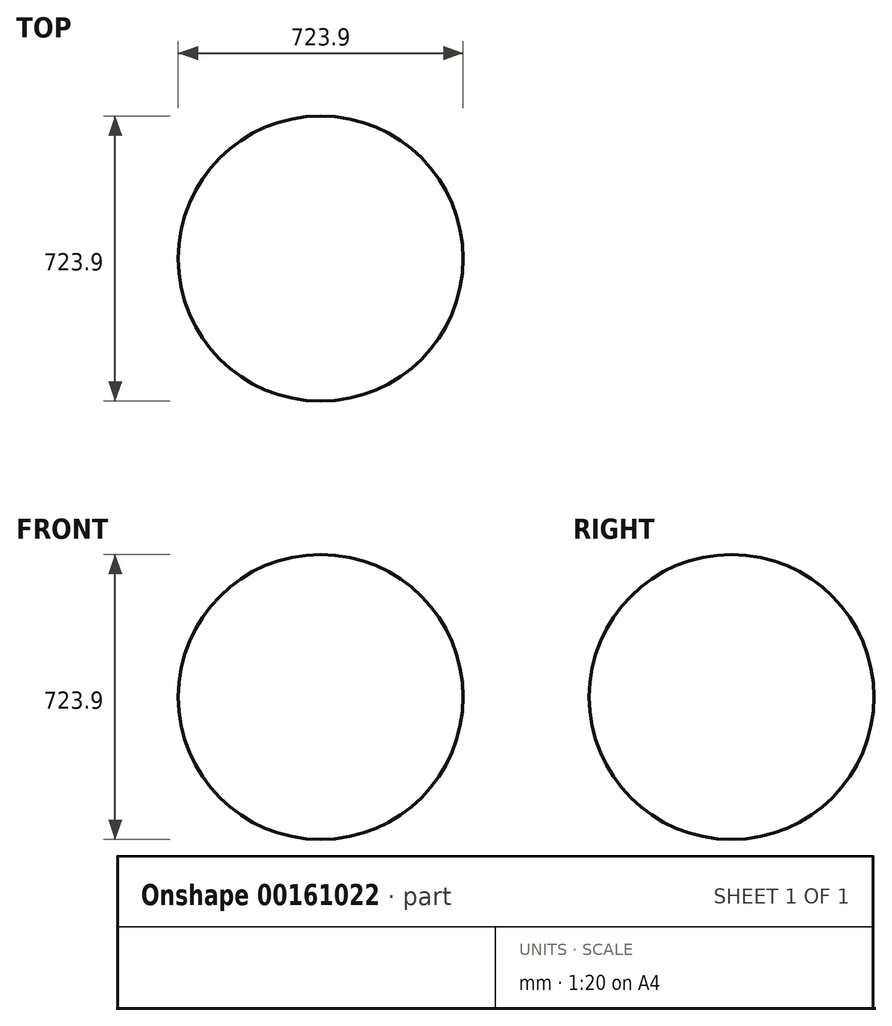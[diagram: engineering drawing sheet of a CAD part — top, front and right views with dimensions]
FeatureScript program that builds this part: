
annotation { "Feature Type Name" : "Feature", "Feature Type Description" : "" }
export const myFeature = defineFeature(function(context is Context, id is Id, definition is map)
    precondition{}
    {
        {
            var Q0;
            Q0=qCreatedBy(makeId("Front.planeOp"),FACE);
            var sketch = newSketch(context, id + "F0", { "sketchPlane" : qUnion([Q0])});
            skArc(sketch, "E0", {"start": v(0, -361.95) * mm, "mid": v(361.95, 0) * mm, "end": v(0, 361.95) * mm});
            skLineSegment(sketch, "E1", {"start": v(0, 1153.47) * mm, "end": v(0, -795.63) * mm});
            skSolve(sketch);
        }
        {
            var Q0;
            {var subQ0=sQuery(id+"F0.wireOp",EDGE,"E0");Q0=makeQuery(id+"F0.imprint","IMPRINT",FACE,{"disambiguationData":[TD([[makeQuery(id+"F0.imprint","IMPRINT",EDGE,{"derivedFrom":subQ0}),1.0]])]});}
            var Q1;
            Q1=sQuery(id+"F0.wireOp",EDGE,"E1");
            revolve(context, id + "F1", {"entities" : qUnion([Q0]), "axis" : qUnion([Q1]), "revolveType" : RevolveType.FULL});
        }
    });
